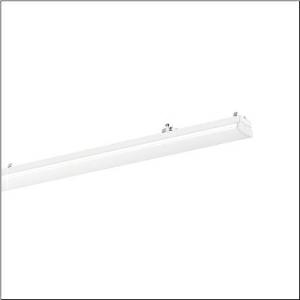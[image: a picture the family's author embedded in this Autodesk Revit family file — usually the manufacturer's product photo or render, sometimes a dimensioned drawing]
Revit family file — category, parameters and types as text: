
# Revit family: licross_r__11_recessed_opal_mo_51te1ddn495g_8c71
name_source: partatom
category: Lighting Fixtures
units: mm (PartAtom-declared; Revit-internal decimal feet)

## family parameters
Cut with Voids When Loaded = No
Host = Face
Light Source = No
Part Type = Normal
Room Calculation Point = No
Round Connector Dimension = Use Diameter
Shared = No

## types (1)
- --- (1 x LED, 9710 lm, 56.7 W, 4000K)
    Apparent Load = 57 VA
    CIE Flux Codes = 44 73 91 87 100
    Color Rendering = 80
    Color Temperature = 4000K
    Default Elevation = 1800 mm
    Description = Licross® 11 recessed opal MO, luminaire insert, of sheet steel, coil coated, white, length: 1.500mm, width: 76mm, height: 87mm, LED rated luminous flux: 9.710lm, light colour: 840, control gear: DALI 2, with plug, 5-pole, with phase selection, mains connection: 220..240V, AC, 50/60Hz, rated input power: 57W, internal wiring halogen-free, primary optical cover: cover, of PMMA, light emission: direct with ceiling illumination distribution, primary light characteristic: symmetric, protection rating (complete): IP54, insulation class (complete): insulation class I (protective earthing), certification: CE, ENEC, VDE, UKCA, protection symbol: D if used in an environment with non-conductive dust loads with corresponding accessories, impact resistance: IK06, permissible ambient temperature for indoor applications: -25..+35°C, corresponds to IFS (International Featured Standards) requirements for safety and quality in the food industry, reducing of maximum allowable ambient temperature of 5°C with ceiling mounting, LABS conformity tested according to VDMA 24364:2018-05, packaging unit: 1 piece
    Height = 83 mm
    Lamp = 1 x LED
    Lamp Light Flux = 9710 lm
    Lamp Power = 56.7 W
    Lamp count = 1
    Length = 1500 mm
    Luminous efficacy = 171 lm/W
    Manufacturer = Siteco
    ModVariant = No
    Model = 51TE1DDN495G
    Mounting Place = Ceiling
    Mounting Type = Pendant
    Number of Poles = 1
    OnlyDefault = Yes
    Power Factor = 1
    Product Name = Licross® 11 recessed opal MO
    Product group = luminaire insert | ceiling pendant
    ProductGroupID = 902
    Protection Class = Protection class I
    Protection Degree = IP 54
    RLX_Detail_Level = 1
    RLX_Emergency_Light_Flux = 0 lm
    RLX_Emergency_Type = 0
    RLX_Emergency_Type_DB = No
    RlxData = <blob elided: 26741 chars, md5=c95348ac>
    Socket = socket
    Standby Power = 0 W
    System Light Flux = 9710 lm
    System Power = 57 W
    Type Comments = factory setting: luminous flux: 100 % | dim-lin: 254 | 378 mA
    Type Image = l_1313666.jpg
    URL = http://relux.com
    VarID = @adj_097469
    Voltage = 0 V
    Weight = 0.00 kg
    Width = 76 mm

## geometry (parser evidence)
native form markers: Blend x4, Sweep x14
no freeform markers — native parametric forms only
